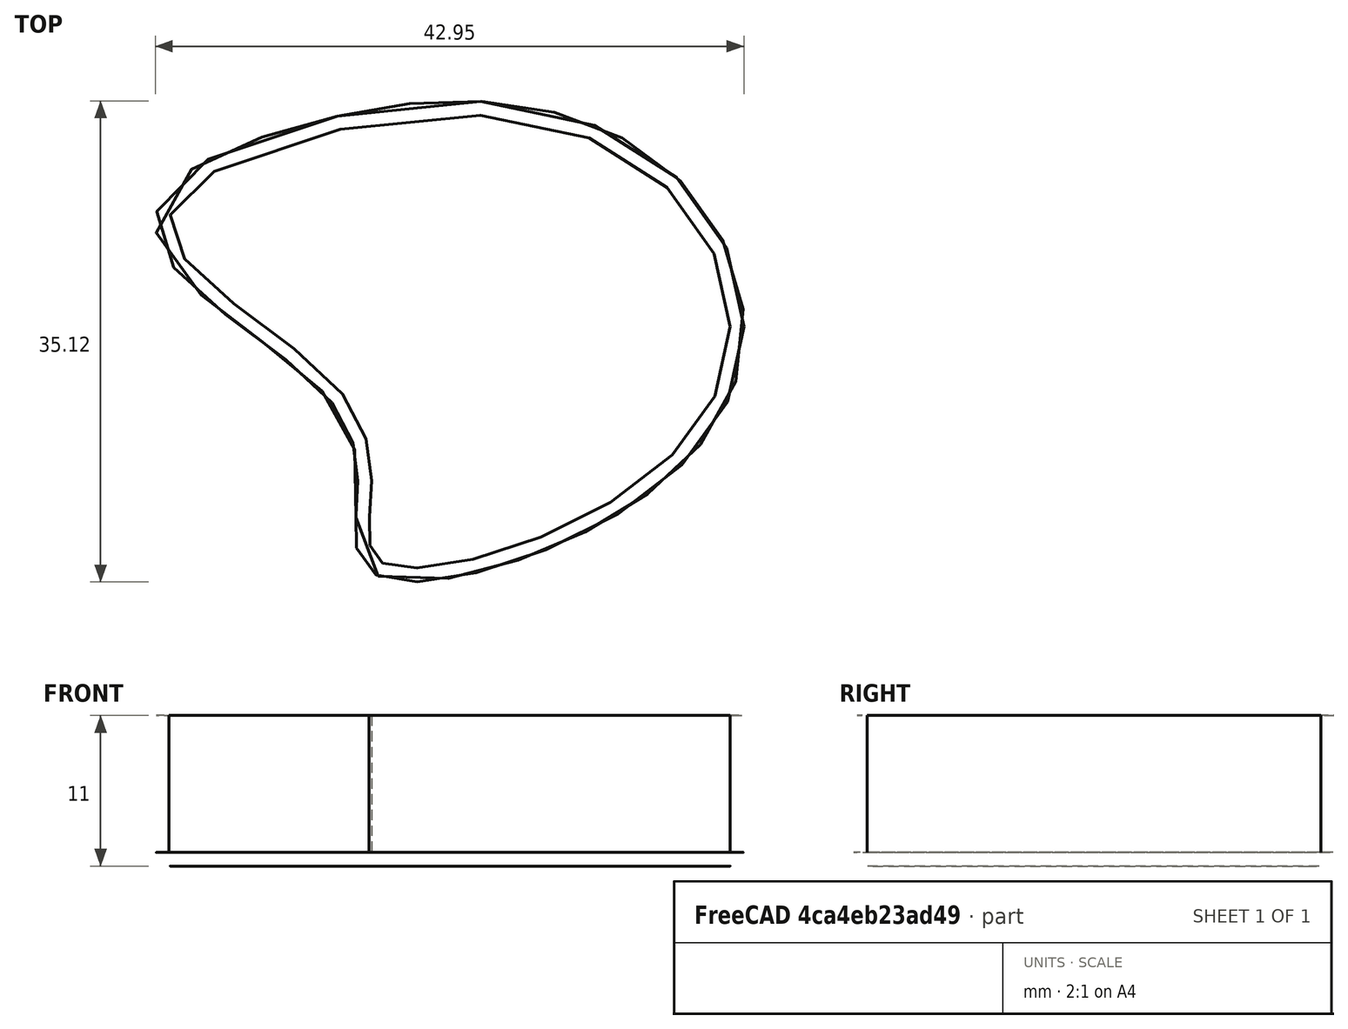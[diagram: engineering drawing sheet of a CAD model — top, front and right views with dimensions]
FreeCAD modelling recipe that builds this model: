
FCSTD DOCUMENT  (FreeCAD 0.17R13217 (Git))
Label: 18-espesor
License: All rights reserved
LicenseURL: http://en.wikipedia.org/wiki/All_rights_reserved
objects: Sketcher::SketchObject×1, PartDesign::Pad×1, PartDesign::Thickness×1, PartDesign::Body×1
note: 5 computed .brp shape members not serialized (recipe doc carries the construction recipe); baked Part::Feature solids carry a one-line shape summary decoded from their .brp

FEATURE [Sketcher::SketchObject] Sketch
  MapMode = 5
  Support = -> [XY_Plane]
  sketch-geometry (13):
    g0-g6: Circle [constr] x7 (B-spline internal-alignment scaffolding for g7; pole/knot coordinates omitted)
    g7: BSplineCurve PolesCount=7 KnotsCount=5 Degree=3 IsPeriodic=0
    g8-g12: GeomPoint [constr] x5 (B-spline internal-alignment scaffolding for g7; pole/knot coordinates omitted)
  constraints (5):
    c: Equal(g0, g1-g6) x6
    c: Coincident(g6,g0)
    c: InternalAlignment(g0-g6 -> g7) x7
    c: InternalAlignment(g8-g12 -> g7) x5
    c: Radius(g3) = 4
FEATURE [PartDesign::Pad] Pad
  Length = 10
  Length2 = 100
  Profile = -> Sketch
  Refine = true
  Type = 0
FEATURE [PartDesign::Thickness] Thickness
  Base = -> Pad [Face3]
  BaseFeature = -> Pad
  Join = 0
  Mode = 0
  Value = 1
FEATURE [PartDesign::Body] Body
  Group = -> [Sketch,Pad,Thickness]
  Origin = -> Origin
  Tip = -> Thickness
